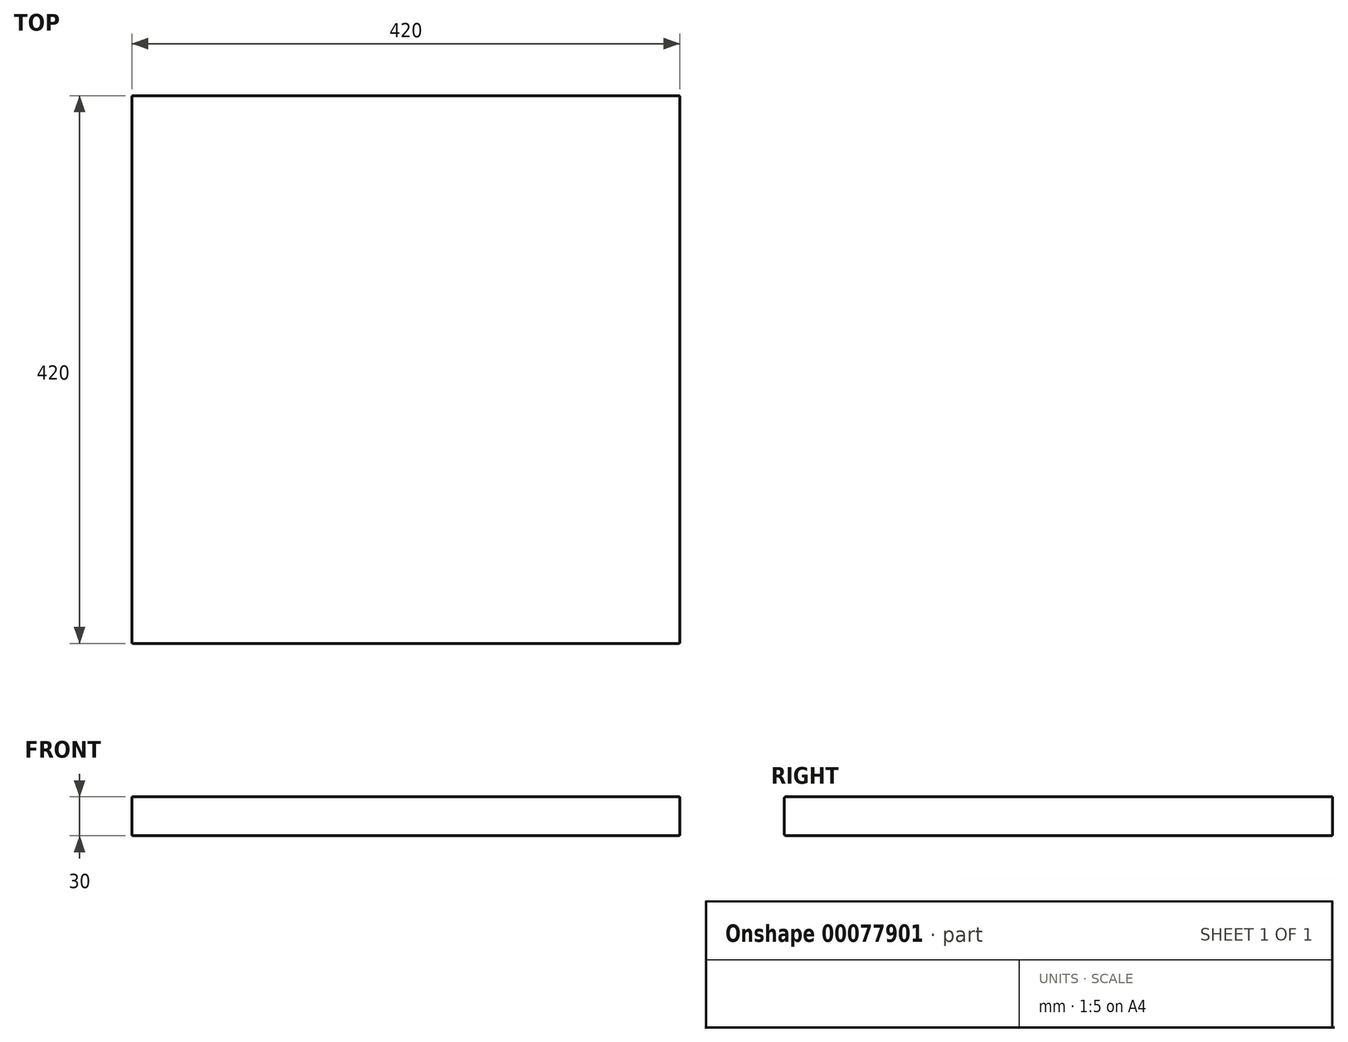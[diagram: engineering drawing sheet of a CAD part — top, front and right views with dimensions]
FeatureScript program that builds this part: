
annotation { "Feature Type Name" : "Feature", "Feature Type Description" : "" }
export const myFeature = defineFeature(function(context is Context, id is Id, definition is map)
    precondition{}
    {
        {
            var Q0;
            Q0=qCreatedBy(makeId("Top.planeOp"),FACE);
            var sketch = newSketch(context, id + "F0", { "sketchPlane" : qUnion([Q0])});
            skLineSegment(sketch, "E0.bottom", {"start": v(0, 0) * mm, "end": v(-420, 0) * mm});
            skLineSegment(sketch, "E0.top", {"start": v(0, 420) * mm, "end": v(-420, 420) * mm});
            skLineSegment(sketch, "E0.left", {"start": v(0, 0) * mm, "end": v(0, 420) * mm});
            skLineSegment(sketch, "E0.right", {"start": v(-420, 0) * mm, "end": v(-420, 420) * mm});
            skSolve(sketch);
        }
        {
            var Q0;
            Q0=makeQuery(id+"F0.imprint","IMPRINT",FACE,{"disambiguationData":[TD([[makeQuery(id+"F0.imprint","IMPRINT",EDGE,{"derivedFrom":sQuery(id+"F0.wireOp",EDGE,"E0.bottom")}),-1.0]])]});
            extrude(context, id + "F1", {"entities" : qUnion([Q0]), "depth" : 30 * mm});
        }
        {
            var Q0;
            Q0=makeQuery(id+"F1.opExtrude","CAP_EDGE",EDGE,{"disambiguationData":[OSD([sQuery(id+"F0.wireOp",EDGE,"E0.bottom")])],"isStart":false});
            var Q1;
            Q1=makeQuery(id+"F1.opExtrude","CAP_EDGE",EDGE,{"disambiguationData":[OSD([sQuery(id+"F0.wireOp",EDGE,"E0.right")])],"isStart":false});
            var Q2;
            Q2=makeQuery(id+"F1.opExtrude","CAP_EDGE",EDGE,{"disambiguationData":[OSD([sQuery(id+"F0.wireOp",EDGE,"E0.top")])],"isStart":false});
            var Q3;
            Q3=makeQuery(id+"F1.opExtrude","CAP_EDGE",EDGE,{"disambiguationData":[OSD([sQuery(id+"F0.wireOp",EDGE,"E0.left")])],"isStart":false});
            var Q4;
            Q4=makeQuery(id+"F1.opExtrude","CAP_EDGE",EDGE,{"disambiguationData":[OSD([sQuery(id+"F0.wireOp",EDGE,"E0.left")])],"isStart":true});
            var Q5;
            Q5=makeQuery(id+"F1.opExtrude","SWEPT_FACE",FACE,{"disambiguationData":[OSD([sQuery(id+"F0.wireOp",EDGE,"E0.bottom")])]});
            var Q6;
            Q6=makeQuery(id+"F1.opExtrude","CAP_EDGE",EDGE,{"disambiguationData":[OSD([sQuery(id+"F0.wireOp",EDGE,"E0.bottom")])],"isStart":true});
            var Q7;
            Q7=makeQuery(id+"F1.opExtrude","SWEPT_EDGE",EDGE,{"disambiguationData":[OSD([sQuery(id+"F0.wireOp",EDGE,"E0.top"),sQuery(id+"F0.wireOp",EDGE,"E0.left")])]});
            var Q8;
            Q8=makeQuery(id+"F1.opExtrude","CAP_FACE",FACE,{"disambiguationData":[OSD([sQuery(id+"F0.wireOp",EDGE,"E0.bottom"),sQuery(id+"F0.wireOp",EDGE,"E0.top"),sQuery(id+"F0.wireOp",EDGE,"E0.left"),sQuery(id+"F0.wireOp",EDGE,"E0.right")])],"isStart":true});
            var Q9;
            Q9=makeQuery(id+"F1.opExtrude","SWEPT_EDGE",EDGE,{"disambiguationData":[OSD([sQuery(id+"F0.wireOp",EDGE,"E0.top"),sQuery(id+"F0.wireOp",EDGE,"E0.right")])]});
            fillet(context, id + "F2", {"entities" : qUnion([Q0, Q1, Q2, Q3, Q4, Q5, Q6, Q7, Q8, Q9]), "radius" : 1 * mm, "tangentPropagation" : true, "allowEdgeOverflow" : false});
        }
    });
